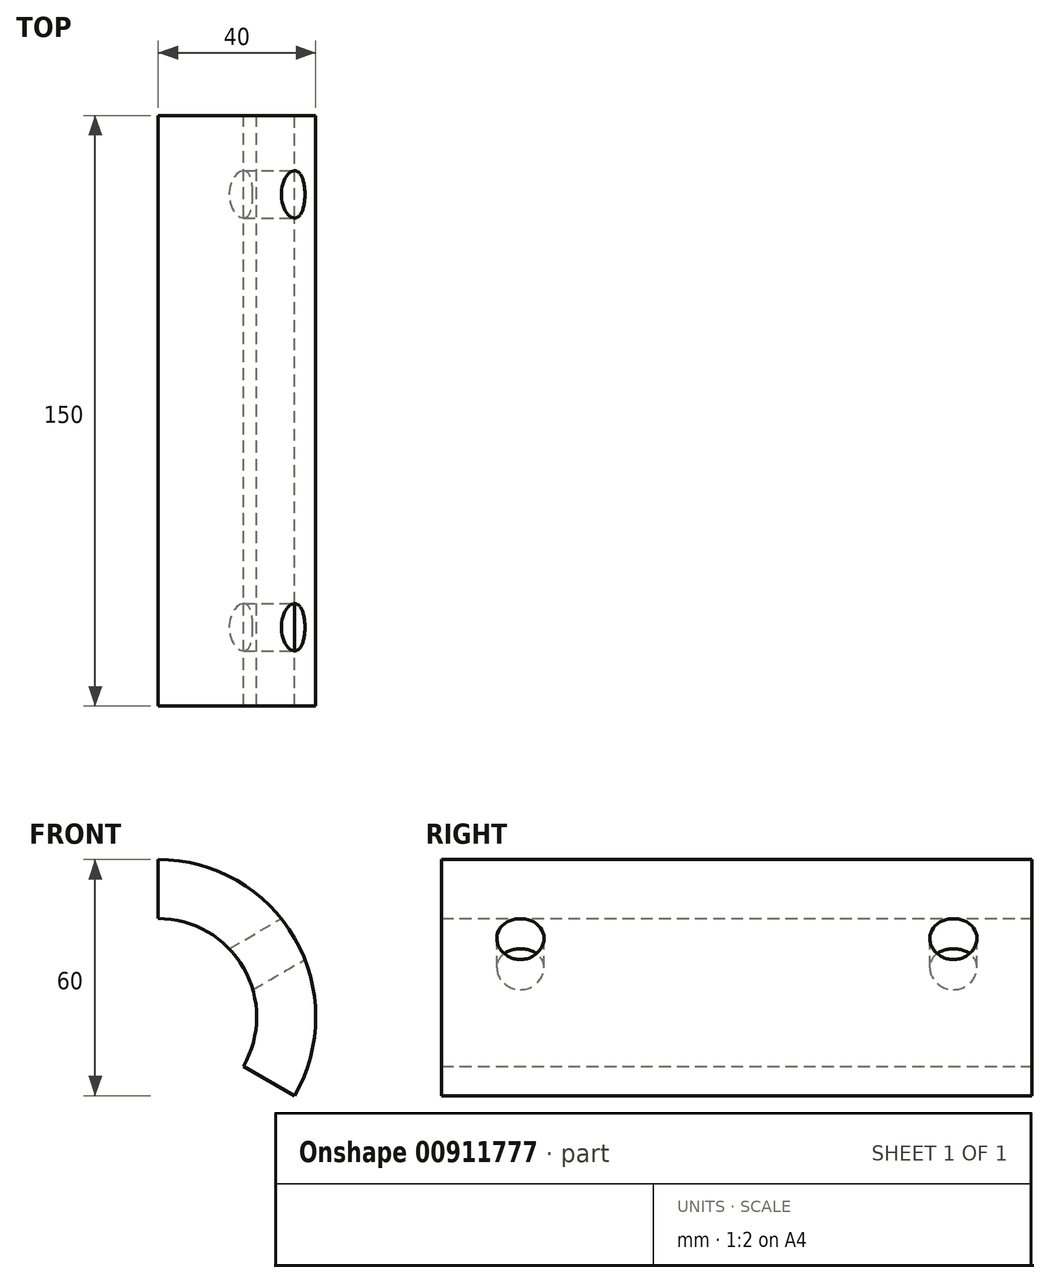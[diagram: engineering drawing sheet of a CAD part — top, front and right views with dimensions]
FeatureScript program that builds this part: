
annotation { "Feature Type Name" : "Feature", "Feature Type Description" : "" }
export const myFeature = defineFeature(function(context is Context, id is Id, definition is map)
    precondition{}
    {
        {
            var Q0;
            Q0=qCreatedBy(makeId("Front.planeOp"),FACE);
            var sketch = newSketch(context, id + "F0", { "sketchPlane" : qUnion([Q0])});
            skCircle(sketch, "E0", {"center": v(0, 0) * mm, "radius": 40 * mm});
            skCircle(sketch, "E1", {"center": v(0, 0) * mm, "radius": 25 * mm});
            skLineSegment(sketch, "E2", {"start": v(0, 0) * mm, "end": v(0, 40) * mm});
            skLineSegment(sketch, "E3", {"start": v(0, 0) * mm, "end": v(34.64, -20) * mm});
            skLineSegment(sketch, "E4", {"start": v(0, 0) * mm, "end": v(34.64, 20) * mm});
            skSolve(sketch);
        }
        {
            var Q0;
            {var subQ0=sQuery(id+"F0.wireOp",EDGE,"E2");var subQ1=sQuery(id+"F0.wireOp",EDGE,"E0");var subQ2=makeQuery(id+"F0.imprint","INTERSECT",VERTEX,{"derivedFrom":[subQ1,subQ0]});Q0=makeQuery(id+"F0.imprint","IMPRINT",FACE,{"disambiguationData":[TD([[makeQuery(id+"F0.imprint","IMPRINT",EDGE,{"disambiguationData":[TD([[subQ2,1.0]])],"derivedFrom":subQ1}),1.0]])]});}
            var Q1;
            {var subQ0=sQuery(id+"F0.wireOp",EDGE,"E3");var subQ1=sQuery(id+"F0.wireOp",EDGE,"E0");var subQ2=makeQuery(id+"F0.imprint","INTERSECT",VERTEX,{"derivedFrom":[subQ1,subQ0]});Q1=makeQuery(id+"F0.imprint","IMPRINT",FACE,{"disambiguationData":[TD([[makeQuery(id+"F0.imprint","IMPRINT",EDGE,{"disambiguationData":[TD([[subQ2,-1.0]])],"derivedFrom":subQ1}),1.0]])]});}
            extrude(context, id + "F1", {"entities" : qUnion([Q0, Q1]), "depth" : 150 * mm, "offsetDistance" : 25 * mm, "symmetric" : true});
        }
        {
            var Q0;
            Q0=sQuery(id+"F0.wireOp",VERTEX,"E4.end");
            var Q1;
            Q1=sQuery(id+"F0.wireOp",VERTEX,"E2.start");
            cPlane(context, id + "F2", {"entities" : qUnion([Q0, Q1]), "cplaneType" : CPlaneType.MID_PLANE, "offset" : 25 * mm, "width" : 150 * mm, "height" : 150 * mm});
        }
        {
            var Q0;
            Q0=qCreatedBy(id+"F2.planeOp",FACE);
            cPlane(context, id + "F3", {"entities" : qUnion([Q0]), "cplaneType" : CPlaneType.OFFSET, "offset" : 20 * mm, "oppositeDirection" : true, "width" : 150 * mm, "height" : 150 * mm});
        }
        {
            var Q0;
            Q0=qCreatedBy(id+"F3.planeOp",FACE);
            var sketch = newSketch(context, id + "F4", { "sketchPlane" : qUnion([Q0])});
            skLineSegment(sketch, "E5", {"start": v(0, 0) * mm, "end": v(-75, 0) * mm});
            skLineSegment(sketch, "E6", {"start": v(-75, 0) * mm, "end": v(0, 0) * mm});
            skLineSegment(sketch, "E7", {"start": v(75, 0) * mm, "end": v(0, 0) * mm});
            skPoint(sketch, "E8", {"position": v(-55, 0) * mm});
            skPoint(sketch, "E9", {"position": v(55, 0) * mm});
            skSolve(sketch);
        }
        {
            var Q0;
            Q0=sQuery(id+"F4.wireOp",VERTEX,"E9");
            var Q1;
            Q1=sQuery(id+"F4.wireOp",VERTEX,"E8");
            var Q2;
            Q2=makeQuery(id+"F1.opExtrude","SWEPT_BODY",BODY,{"disambiguationData":[OSD([sQuery(id+"F0.wireOp",EDGE,"E0"),sQuery(id+"F0.wireOp",EDGE,"E1"),sQuery(id+"F0.wireOp",EDGE,"E2"),sQuery(id+"F0.wireOp",EDGE,"E3")])]});
            hole(context, id + "F5", {"style" : HoleStyle.SIMPLE, "endStyle" : HoleEndStyle.THROUGH, "oppositeDirection" : true, "holeDiameter" : 12 * mm, "majorDiameter" : 5 * mm, "isTappedThrough" : true, "tappedDepth" : 12 * mm, "tapClearance" : 3, "locations" : qUnion([Q0, Q1]), "scope" : qUnion([Q2])});
        }
    });
